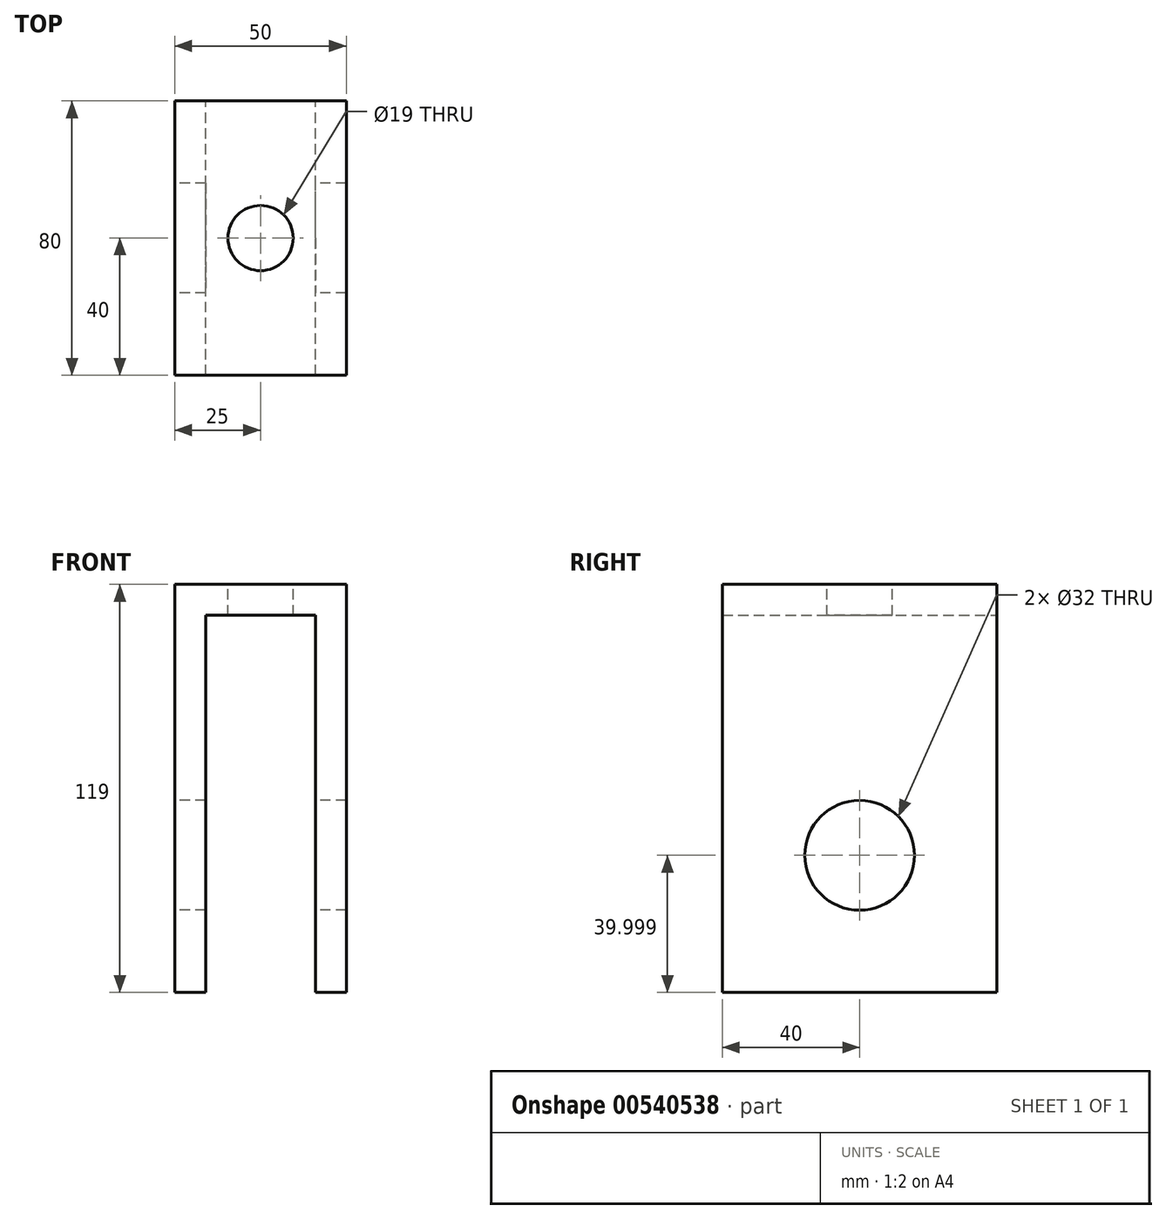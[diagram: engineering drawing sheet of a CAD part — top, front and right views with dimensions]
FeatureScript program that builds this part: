
annotation { "Feature Type Name" : "Feature", "Feature Type Description" : "" }
export const myFeature = defineFeature(function(context is Context, id is Id, definition is map)
    precondition{}
    {
        {
            var Q0;
            Q0=qCreatedBy(makeId("Front.planeOp"),FACE);
            var sketch = newSketch(context, id + "F0", { "sketchPlane" : qUnion([Q0])});
            skLineSegment(sketch, "E0", {"start": v(-20.88, 26.3) * mm, "end": v(-20.88, 136.3) * mm});
            skLineSegment(sketch, "E1", {"start": v(-20.88, 136.3) * mm, "end": v(11.12, 136.3) * mm});
            skLineSegment(sketch, "E2", {"start": v(11.12, 136.3) * mm, "end": v(11.12, 26.3) * mm});
            skLineSegment(sketch, "E3", {"start": v(11.12, 26.3) * mm, "end": v(20.12, 26.3) * mm});
            skLineSegment(sketch, "E4", {"start": v(20.12, 26.3) * mm, "end": v(20.12, 145.3) * mm});
            skLineSegment(sketch, "E5", {"start": v(20.12, 145.3) * mm, "end": v(-29.88, 145.3) * mm});
            skLineSegment(sketch, "E6", {"start": v(-29.88, 145.3) * mm, "end": v(-29.88, 26.3) * mm});
            skLineSegment(sketch, "E7", {"start": v(-29.88, 26.3) * mm, "end": v(-20.88, 26.3) * mm});
            skSolve(sketch);
        }
        {
            var Q0;
            Q0 = qSketchRegion(id + "F0", true);
            extrude(context, id + "F1", {"entities" : qUnion([Q0]), "depth" : 80 * mm, "offsetDistance" : 25 * mm});
        }
        {
            var Q0;
            Q0=makeQuery(id+"F1.opExtrude","SWEPT_FACE",FACE,{"disambiguationData":[OSD([sQuery(id+"F0.wireOp",EDGE,"E6")])]});
            var sketch = newSketch(context, id + "F2", { "sketchPlane" : qUnion([Q0])});
            skCircle(sketch, "E8", {"center": v(40, 66.3) * mm, "radius": 16 * mm});
            skPoint(sketch, "E8.centerSnap0", {"position": v(40, 26.3) * mm});
            skPoint(sketch, "E8.perimeterSnap0", {"position": v(40, 26.3) * mm});
            skPoint(sketch, "E8.perimeterSnap1", {"position": v(0, 85.8) * mm});
            skSolve(sketch);
        }
        {
            var Q0;
            Q0 = qSketchRegion(id + "F2", true);
            extrude(context, id + "F3", {"entities" : qUnion([Q0]), "operationType" : NewBodyOperationType.REMOVE, "endBound" : BoundingType.THROUGH_ALL, "oppositeDirection" : true, "depth" : 25 * mm, "offsetDistance" : 25 * mm});
        }
        {
            var Q0;
            Q0=makeQuery(id+"F1.opExtrude","SWEPT_FACE",FACE,{"disambiguationData":[OSD([sQuery(id+"F0.wireOp",EDGE,"E5")])]});
            var sketch = newSketch(context, id + "F4", { "sketchPlane" : qUnion([Q0])});
            skCircle(sketch, "E9", {"center": v(-4.88, -40) * mm, "radius": 9.5 * mm});
            skPoint(sketch, "E9.centerSnap0", {"position": v(20.12, -40) * mm});
            skPoint(sketch, "E9.centerSnap1", {"position": v(-4.88, 0) * mm});
            skSolve(sketch);
        }
        {
            var Q0;
            Q0 = qSketchRegion(id + "F4", true);
            extrude(context, id + "F5", {"entities" : qUnion([Q0]), "operationType" : NewBodyOperationType.REMOVE, "endBound" : BoundingType.THROUGH_ALL, "oppositeDirection" : true, "depth" : 25 * mm, "offsetDistance" : 25 * mm});
        }
    });
